# Revit family: Door-NanaWall-SL-81
name_source: partatom
category: Doors
revit_build: Autodesk Revit Architecture 2013 (Build: 20130531_2115(x64)
units: mm (PartAtom-declared; Revit-internal decimal feet)

## types (1)
- Folding Door
    04 CSI = 08 41 13
    95 CSI = 8411
    Assembly Code = B2030110
    Cost Info = http://www.nanawall.com
    Description = Structurally Glazed Thermally Broken Aluminum Framed Folding System
    Detail Component in Plan = No
    Detail Component in Section = No
    Disclaimer = Please note that the Revit model is for schematic purposes only.  To obtain a detailed 3D model, please go to the NanaWall's configurator at www.nanawall.com.
    Engineering Details URL = http://www.nanawall.com
    Exterior Wall Offset = 0' - 3 1/2"
    Function = Interior
    Glass Material = Glass - NanaWall - Clear
    Glazing Options = http://www.nanawall.com
    Height = 8' - 2"
    Height Constraint = 8' - 2"
    Installation and Service URL = http://www.nanawall.com
    Manufacturer = NanaWall Systems, Inc.
    Manufacturer Fax = (415) 383-0312
    Max Panel Height = 7' - 6 117/128"
    Model = SL-81
    NanaWall Configurator = http://www.nanawall.com
    Opening Width = 9' - 4 127/128"
    Panel Height = 7' - 6 117/128"
    Performance URL = http://www.nanawall.com
    Product Page URL = http://www.nanawall.com
    Rough Height = 7' - 9 15/128"
    Rough Width = 9' - 10 7/64"
    Sash = Metal - NanaWall - Aluminum
    Sills Available = Raised, Low Profile Saddle, Flush
    Subcategory = Folding Door
    Thickness = 0' - 3 19/128"
    U Value = 0.23
    URL = http://www.nanawall.com
    Wall Closure = By host
    Warranty URL = http://www.nanawall.com
    Width = 10' - 0"

## geometry (parser evidence)
native form markers: Blend x4, Sweep x14
no freeform markers — native parametric forms only
